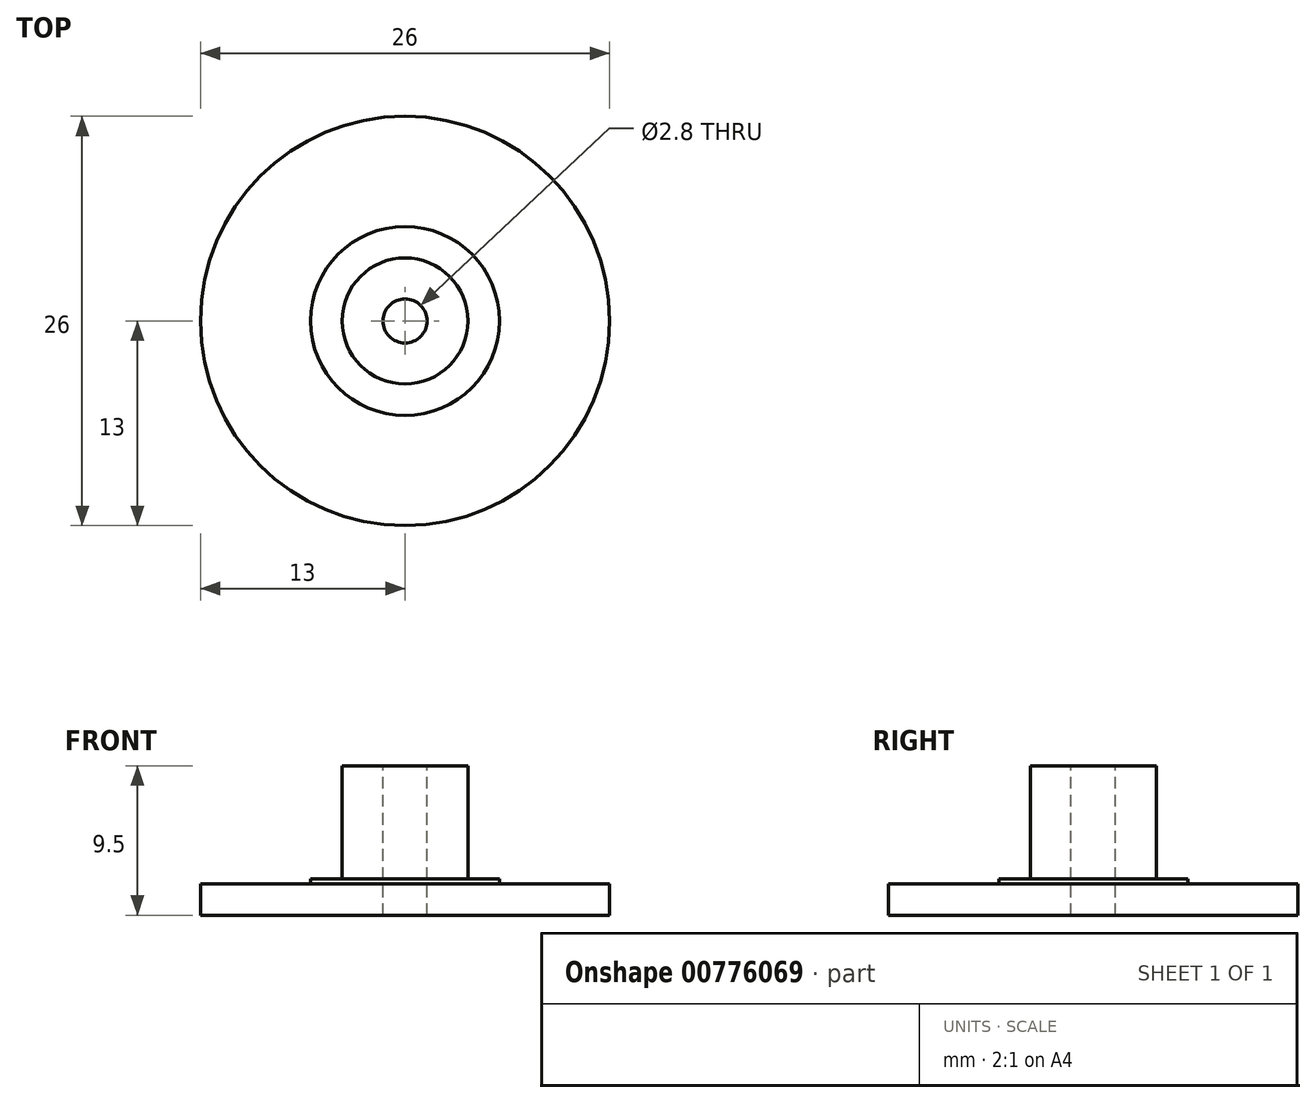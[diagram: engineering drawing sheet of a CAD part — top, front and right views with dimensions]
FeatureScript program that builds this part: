
annotation { "Feature Type Name" : "Feature", "Feature Type Description" : "" }
export const myFeature = defineFeature(function(context is Context, id is Id, definition is map)
    precondition{}
    {
        {
            var Q0;
            Q0=qCreatedBy(makeId("Top.planeOp"),FACE);
            var sketch = newSketch(context, id + "F0", { "sketchPlane" : qUnion([Q0])});
            skCircle(sketch, "E0", {"center": v(0, 0) * mm, "radius": 13 * mm});
            skSolve(sketch);
        }
        {
            var Q0;
            Q0=makeQuery(id+"F0.imprint","IMPRINT",FACE,{"disambiguationData":[TD([[makeQuery(id+"F0.imprint","IMPRINT",EDGE,{"derivedFrom":sQuery(id+"F0.wireOp",EDGE,"E0")}),1.0]])]});
            extrude(context, id + "F1", {"entities" : qUnion([Q0]), "depth" : 2 * mm, "offsetDistance" : 25 * mm});
        }
        {
            var Q0;
            Q0=makeQuery(id+"F1.opExtrude","CAP_FACE",FACE,{"disambiguationData":[OSD([sQuery(id+"F0.wireOp",EDGE,"E0")])],"isStart":false});
            var sketch = newSketch(context, id + "F2", { "sketchPlane" : qUnion([Q0])});
            skCircle(sketch, "E1.0.0", {"center": v(0, 0) * mm, "radius": 13 * mm});
            skCircle(sketch, "E2", {"center": v(0, 0) * mm, "radius": 6 * mm});
            skSolve(sketch);
        }
        {
            var Q0;
            Q0=makeQuery(id+"F2.imprint","IMPRINT",FACE,{"disambiguationData":[TD([[makeQuery(id+"F2.imprint","IMPRINT",EDGE,{"derivedFrom":sQuery(id+"F2.wireOp",EDGE,"E2")}),1.0]])]});
            extrude(context, id + "F3", {"entities" : qUnion([Q0]), "operationType" : NewBodyOperationType.ADD, "depth" : .3 * mm, "offsetDistance" : 25 * mm});
        }
        {
            var Q0;
            Q0=makeQuery(id+"F3.opExtrude","CAP_FACE",FACE,{"disambiguationData":[OSD([sQuery(id+"F2.wireOp",EDGE,"E2")])],"isStart":false});
            var sketch = newSketch(context, id + "F4", { "sketchPlane" : qUnion([Q0])});
            skCircle(sketch, "E3.0.0", {"center": v(0, 0) * mm, "radius": 6 * mm});
            skCircle(sketch, "E4", {"center": v(0, 0) * mm, "radius": 4 * mm});
            skSolve(sketch);
        }
        {
            var Q0;
            Q0=makeQuery(id+"F4.imprint","IMPRINT",FACE,{"disambiguationData":[TD([[makeQuery(id+"F4.imprint","IMPRINT",EDGE,{"derivedFrom":sQuery(id+"F4.wireOp",EDGE,"E4")}),1.0]])]});
            extrude(context, id + "F5", {"entities" : qUnion([Q0]), "operationType" : NewBodyOperationType.ADD, "depth" : 7.2 * mm, "offsetDistance" : 25 * mm});
        }
        {
            var Q0;
            Q0=makeQuery(id+"F5.opExtrude","CAP_FACE",FACE,{"disambiguationData":[OSD([sQuery(id+"F4.wireOp",EDGE,"E4")])],"isStart":false});
            var sketch = newSketch(context, id + "F6", { "sketchPlane" : qUnion([Q0])});
            skCircle(sketch, "E5.0.0", {"center": v(0, 0) * mm, "radius": 4 * mm});
            skCircle(sketch, "E6", {"center": v(0, 0) * mm, "radius": 1.4 * mm});
            skSolve(sketch);
        }
        {
            var Q0;
            Q0=makeQuery(id+"F6.imprint","IMPRINT",FACE,{"disambiguationData":[TD([[makeQuery(id+"F6.imprint","IMPRINT",EDGE,{"derivedFrom":sQuery(id+"F6.wireOp",EDGE,"E6")}),1.0]])]});
            extrude(context, id + "F7", {"entities" : qUnion([Q0]), "operationType" : NewBodyOperationType.REMOVE, "endBound" : BoundingType.THROUGH_ALL, "oppositeDirection" : true, "depth" : 25 * mm, "offsetDistance" : 25 * mm});
        }
    });
